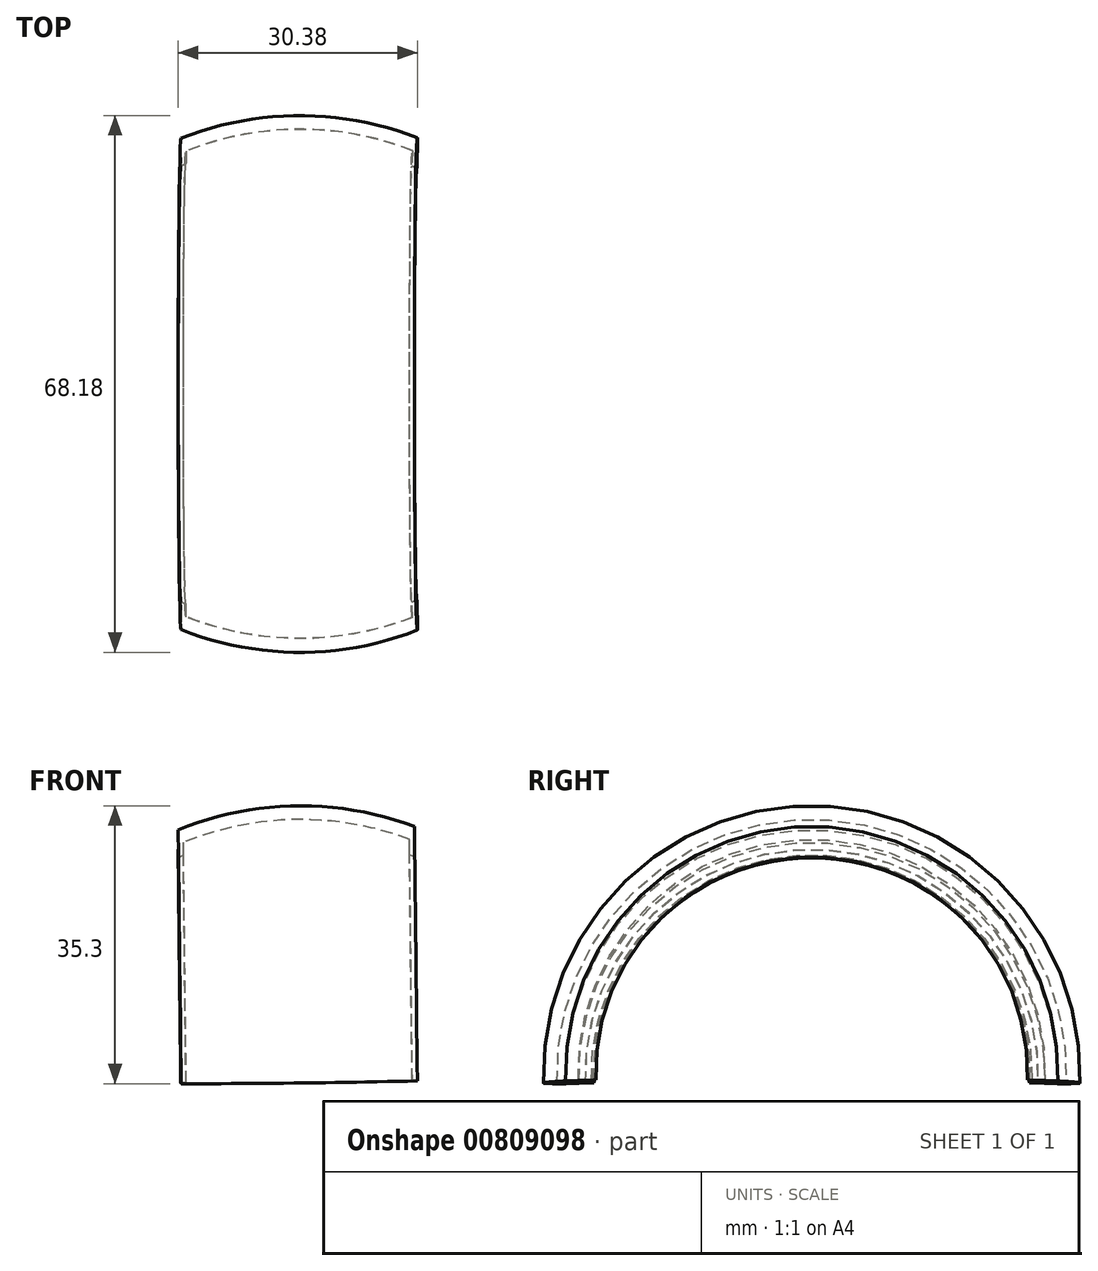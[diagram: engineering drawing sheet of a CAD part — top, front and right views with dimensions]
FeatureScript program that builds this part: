
annotation { "Feature Type Name" : "Feature", "Feature Type Description" : "" }
export const myFeature = defineFeature(function(context is Context, id is Id, definition is map)
    precondition{}
    {
        {
            var Q0;
            Q0=qCreatedBy(makeId("Front.planeOp"),FACE);
            var sketch = newSketch(context, id + "F0", { "sketchPlane" : qUnion([Q0])});
            skLineSegment(sketch, "E0", {"start": v(0, 52.36) * mm, "end": v(0, -40) * mm, "construction": true});
            skLineSegment(sketch, "E1", {"start": v(-15, 39.54) * mm, "end": v(-15, -26.17) * mm});
            skLineSegment(sketch, "E2", {"start": v(15, 52.35) * mm, "end": v(15, 7.63) * mm, "construction": true});
            skLineSegment(sketch, "E3", {"start": v(-40, 6.68) * mm, "end": v(41.42, 7.63) * mm, "construction": true});
            skPoint(sketch, "E3.startSnap0", {"position": v(-15, 6.68) * mm});
            skPoint(sketch, "E3.endSnap0", {"position": v(15, 7.63) * mm});
            skArc(sketch, "E4.trimOffspring", {"start": v(41.42, 7.63) * mm, "mid": v(32.36, 26.66) * mm, "end": v(15, 38.61) * mm});
            skPoint(sketch, "E5.orphan", {"position": v(15, -37.08) * mm});
            skArc(sketch, "E6", {"start": v(-15, 37.98) * mm, "mid": v(-31.58, 25.6) * mm, "end": v(-40, 6.68) * mm});
            skArc(sketch, "E7", {"start": v(15, 38.61) * mm, "mid": v(-0.04, 41.24) * mm, "end": v(-15, 38.2) * mm});
            skLineSegment(sketch, "E8", {"start": v(-15, 6.68) * mm, "end": v(-15, 6.98) * mm});
            skLineSegment(sketch, "E9", {"start": v(-15, 37.98) * mm, "end": v(-15, 6.98) * mm});
            skLineSegment(sketch, "E10.0", {"start": v(-15, 39.54) * mm, "end": v(-15, -6.53) * mm});
            skLineSegment(sketch, "E11.0", {"start": v(15, 52.35) * mm, "end": v(15, 7.37) * mm, "construction": true});
            skLineSegment(sketch, "E12", {"start": v(15, 38.61) * mm, "end": v(15, 8.78) * mm});
            skLineSegment(sketch, "E13", {"start": v(15, 38.61) * mm, "end": v(15, 7.34) * mm});
            skArc(sketch, "E14.0", {"start": v(14.39, 36.98) * mm, "mid": v(-0.02, 39.5) * mm, "end": v(-14.34, 36.58) * mm});
            skLineSegment(sketch, "E15", {"start": v(14.39, 36.98) * mm, "end": v(14.39, 35.02) * mm});
            skLineSegment(sketch, "E16", {"start": v(14.39, 35.02) * mm, "end": v(16.78, 34.02) * mm});
            skLineSegment(sketch, "E17", {"start": v(16.78, 34.02) * mm, "end": v(16.78, 35.05) * mm});
            skLineSegment(sketch, "E18", {"start": v(16.78, 35.05) * mm, "end": v(15, 35.97) * mm});
            skLineSegment(sketch, "E19", {"start": v(15, 35.97) * mm, "end": v(15, 38.61) * mm});
            skLineSegment(sketch, "E20", {"start": v(-14.34, 36.58) * mm, "end": v(-14.34, 35) * mm});
            skLineSegment(sketch, "E21", {"start": v(-14.34, 35) * mm, "end": v(-15.57, 34.34) * mm});
            skLineSegment(sketch, "E22", {"start": v(-15.57, 34.34) * mm, "end": v(-15.9, 35.25) * mm});
            skLineSegment(sketch, "E23", {"start": v(-15.9, 35.25) * mm, "end": v(-14.95, 35.73) * mm});
            skLineSegment(sketch, "E24", {"start": v(-14.95, 35.73) * mm, "end": v(-15, 38.2) * mm});
            skSolve(sketch);
        }
        {
            var Q0;
            Q0=makeQuery(id+"F0.imprint","IMPRINT",FACE,{"disambiguationData":[TD([[makeQuery(id+"F0.imprint","IMPRINT",EDGE,{"derivedFrom":sQuery(id+"F0.wireOp",EDGE,"E7")}),1.0]])]});
            var Q1;
            Q1=sQuery(id+"F0.wireOp",EDGE,"E3");
            revolve(context, id + "F1", {"surfaceOperationType" : NewSurfaceOperationType.NEW, "entities" : qUnion([Q0]), "axis" : qUnion([Q1]), "revolveType" : RevolveType.SYMMETRIC, "angle" : 183.78 * degree});
        }
    });
